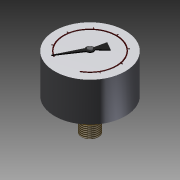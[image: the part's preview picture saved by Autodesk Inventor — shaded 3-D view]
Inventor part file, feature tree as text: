
AUTODESK INVENTOR PART (.ipt)
format: ipt  version: 2011 (Build 150239000, 239)  size: 151,552 bytes
history: native  units: mm
features: imported_body x1, thread x1
ambient origin geometry x8: Origin, YZ Plane, XZ Plane, XY Plane, X Axis, Y Axis, Z Axis, Center Point
bodies: Solid1 (feature_tree)
feature tree (2):
  imported_body  "Base1"
  thread  "Thread1"  [1 undecoded]
note: 1 required parameter value undecoded (feature->parameter linkage not recoverable at this tier; creation-order binding heuristic only, values carry confidence <= 0.55)
